# Revit family: Faucet-Lavatory-KOHLER-Aleo-K-25104T_1
name_source: partatom
category: Plumbing Fixtures
units: mm (PartAtom-declared; Revit-internal decimal feet)

## family parameters
Cut with Voids When Loaded = No
Host = Face
OmniClass Number = 23.31.11.00
OmniClass Title = Faucets
Part Type = Normal
Room Calculation Point = No
Round Connector Dimension = Use Diameter
Shared = No

## types (6) — shared parameters
ADA Compliant = No
Assembly Code = D2010
CW Connection = Yes
Cold Water Inlet = Cold Water Inlet
Date Modified = 11/16/2022
Default Elevation = 36"
Drain Included = Yes
Faucet Hole Spacing = 0"
Flow Rate = 2 GPM
HW Connection = Yes
Handle Clearance = 3 7/16"
Height = 12 9/16"
Hot Water Inlet = Hot Water Inlet
Length = 5 15/16"
Manufacturer = Kohler Co.
Master Format 2014 = 22 41 39
Master Format 2014 Name = Residential Faucets, Supplies, and Trim
Material = Premium Metal Construction
Pressure = 0.00 psi
Product Name = Aleo S
Spout Reach = 5 15/16"
URL = http://www.kohler.com.cn
Vent Connection = No
Waste Connection = No
Waste Water Outlet = Waste Water Outlet
WaterSense Certified = No
Width = 1 7/8"

## per-type parameters (varying)
| type | Description | Finish | Handle | Lever | Model | Product Documentation Link | Product Page URL | Type |
| Handle, 2BL-Black | Leo single lever bowl faucet with high spout (ingenious style) | KOHLER-Metal-2BL-Black | Yes | No | K-25104T-4-2BL | https://files.kohler.com.cn | https://www.kohler.com.cn | 1 |
| Handle, BL-Matte Black | Leo single lever bowl faucet with high spout (ingenious style) | Kohler-Metal-BL-Matte_Black | Yes | No | K-25104T-4-BL | https://files.kohler.com.cn |  | 2 |
| Handle, CP-Polished Chrome | Leo single lever bowl faucet with high spout (ingenious style) | Kohler-Metal-CP-Polished_Chrome | Yes | No | K-25104T-4-CP | https://files.kohler.com.cn | https://www.kohler.com.cn | 3 |
| Lever Handle, 2BL-Black | Super Tall Single Control Lavatory Faucet OL | KOHLER-Metal-2BL-Black | No | Yes | K-25104T-4F-2BL |  |  | 4 |
| Lever Handle, BL-Matte Black | Super Tall Single Control Lavatory Faucet OL | Kohler-Metal-BL-Matte_Black | No | Yes | K-25104T-4F-BL |  |  | 5 |
| Lever Handle, CP-Polished Chrome | Super Tall Single Control Lavatory Faucet OL | Kohler-Metal-CP-Polished_Chrome | No | Yes | K-25104T-4F-CP |  |  | 6 |

## geometry (parser evidence)
native form markers: Sweep x4
no freeform markers — native parametric forms only
